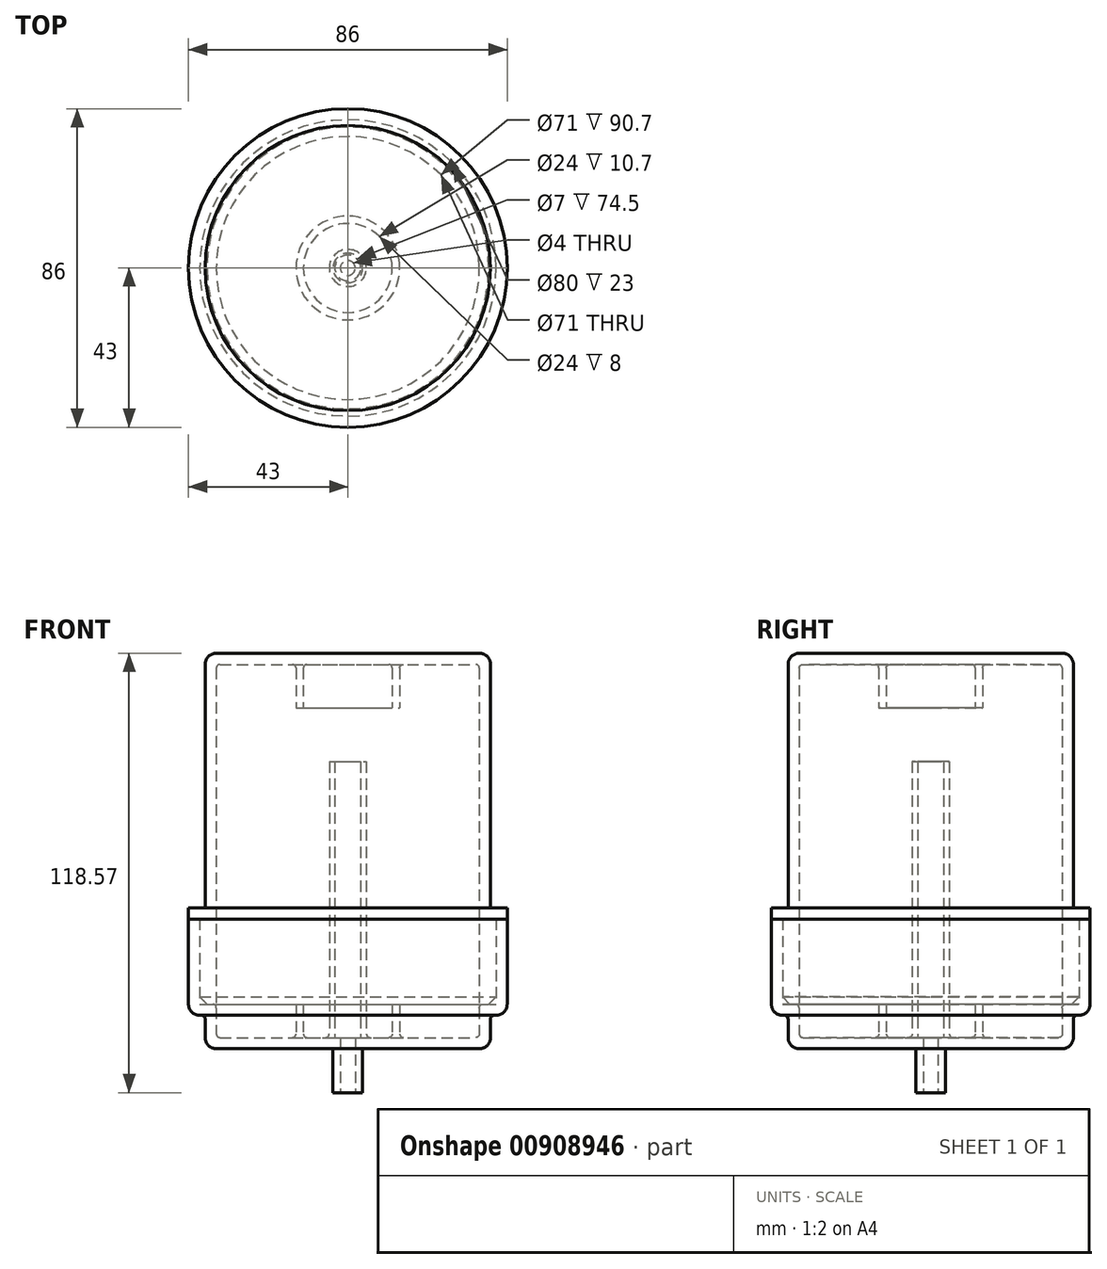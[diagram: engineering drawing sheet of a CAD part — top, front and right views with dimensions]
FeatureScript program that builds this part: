
annotation { "Feature Type Name" : "Feature", "Feature Type Description" : "" }
export const myFeature = defineFeature(function(context is Context, id is Id, definition is map)
    precondition{}
    {
        {
            var Q0;
            Q0=qCreatedBy(makeId("Front.planeOp"),FACE);
            var sketch = newSketch(context, id + "F0", { "sketchPlane" : qUnion([Q0])});
            skLineSegment(sketch, "E0", {"start": v(0, 0) * mm, "end": v(0, 111.4) * mm, "construction": true});
            skLineSegment(sketch, "E1", {"start": v(12, 1) * mm, "end": v(12, 9) * mm});
            skLineSegment(sketch, "E2", {"start": v(12, 9) * mm, "end": v(14, 9) * mm});
            skLineSegment(sketch, "E3", {"start": v(14, 9) * mm, "end": v(14, 1) * mm});
            skLineSegment(sketch, "E4", {"start": v(15, 0) * mm, "end": v(34.5, 0) * mm});
            skLineSegment(sketch, "E5", {"start": v(35.5, 1) * mm, "end": v(35.5, 8) * mm});
            skLineSegment(sketch, "E6", {"start": v(36.5, 9) * mm, "end": v(40, 9) * mm});
            skLineSegment(sketch, "E7", {"start": v(35.5, -3) * mm, "end": v(4, -3) * mm});
            skLineSegment(sketch, "E8", {"start": v(40, 9) * mm, "end": v(40, 32) * mm});
            skLineSegment(sketch, "E9", {"start": v(40, 32) * mm, "end": v(43, 32) * mm});
            skLineSegment(sketch, "E10", {"start": v(43, 32) * mm, "end": v(43, 9) * mm});
            skLineSegment(sketch, "E11", {"start": v(40, 6) * mm, "end": v(39.5, 6) * mm});
            skLineSegment(sketch, "E12", {"start": v(38.5, 5) * mm, "end": v(38.5, 0) * mm});
            skLineSegment(sketch, "E13", {"start": v(3.5, 0) * mm, "end": v(3.5, 74.5) * mm});
            skLineSegment(sketch, "E14", {"start": v(3.5, 74.5) * mm, "end": v(5, 74.5) * mm});
            skLineSegment(sketch, "E15", {"start": v(5, 74.5) * mm, "end": v(5, 1) * mm});
            skLineSegment(sketch, "E16.trimOffspring", {"start": v(6, 0) * mm, "end": v(11, 0) * mm});
            skPoint(sketch, "E17.visualSharp", {"position": v(38.5, -3) * mm});
            skArc(sketch, "E17.filletArc", {"start": v(35.5, -3) * mm, "mid": v(37.62, -2.12) * mm, "end": v(38.5, 0) * mm});
            skPoint(sketch, "E18.visualSharp", {"position": v(43, 6) * mm});
            skArc(sketch, "E18.filletArc", {"start": v(40, 6) * mm, "mid": v(42.12, 6.88) * mm, "end": v(43, 9) * mm});
            skPoint(sketch, "E19.visualSharp", {"position": v(5, 0) * mm});
            skArc(sketch, "E19.filletArc", {"start": v(5, 1) * mm, "mid": v(5.3, 0.3) * mm, "end": v(6, 0) * mm});
            skPoint(sketch, "E20.visualSharp", {"position": v(12, 0) * mm});
            skArc(sketch, "E20.filletArc", {"start": v(11, 0) * mm, "mid": v(11.7, 0.3) * mm, "end": v(12, 1) * mm});
            skPoint(sketch, "E21.visualSharp", {"position": v(14, 0) * mm});
            skArc(sketch, "E21.filletArc", {"start": v(14, 1) * mm, "mid": v(14.3, 0.3) * mm, "end": v(15, 0) * mm});
            skPoint(sketch, "E22.visualSharp", {"position": v(35.5, 9) * mm});
            skArc(sketch, "E22.filletArc", {"start": v(36.5, 9) * mm, "mid": v(35.8, 8.7) * mm, "end": v(35.5, 8) * mm});
            skPoint(sketch, "E23.visualSharp", {"position": v(38.5, 6) * mm});
            skArc(sketch, "E23.filletArc", {"start": v(39.5, 6) * mm, "mid": v(38.8, 5.7) * mm, "end": v(38.5, 5) * mm});
            skArc(sketch, "E24.filletArc", {"start": v(34.5, 0) * mm, "mid": v(35.2, 0.3) * mm, "end": v(35.5, 1) * mm});
            skLineSegment(sketch, "E25", {"start": v(2, -14.87) * mm, "end": v(4, -14.87) * mm});
            skLineSegment(sketch, "E26", {"start": v(4, -14.87) * mm, "end": v(4, -3) * mm});
            skLineSegment(sketch, "E27", {"start": v(2, -14.87) * mm, "end": v(2, -3) * mm});
            skLineSegment(sketch, "E28", {"start": v(3.5, 0) * mm, "end": v(2, 0) * mm});
            skLineSegment(sketch, "E29", {"start": v(2, -3) * mm, "end": v(2, 0) * mm});
            skLineSegment(sketch, "E30", {"start": v(0, 0) * mm, "end": v(2, 0) * mm});
            skSolve(sketch);
        }
        {
            var Q0;
            Q0=makeQuery(id+"F0.imprint","IMPRINT",FACE,{"disambiguationData":[TD([[makeQuery(id+"F0.imprint","IMPRINT",EDGE,{"derivedFrom":sQuery(id+"F0.wireOp",EDGE,"E1")}),-1.0]])]});
            var Q1;
            Q1=sQuery(id+"F0.wireOp",EDGE,"E0");
            revolve(context, id + "F1", {"surfaceOperationType" : NewSurfaceOperationType.NEW, "entities" : qUnion([Q0]), "axis" : qUnion([Q1]), "revolveType" : RevolveType.FULL});
        }
        {
            var Q0;
            Q0=qCreatedBy(makeId("Front.planeOp"),FACE);
            var sketch = newSketch(context, id + "F2", { "sketchPlane" : qUnion([Q0])});
            skLineSegment(sketch, "E31.0", {"start": v(36.5, 9) * mm, "end": v(38, 9) * mm});
            skLineSegment(sketch, "E31.1", {"start": v(40, 11) * mm, "end": v(40, 32) * mm});
            skLineSegment(sketch, "E32", {"start": v(36.5, 9) * mm, "end": v(35.5, 9) * mm});
            skLineSegment(sketch, "E33", {"start": v(35.5, 9) * mm, "end": v(35.5, 99.7) * mm});
            skLineSegment(sketch, "E34.0", {"start": v(40, 32) * mm, "end": v(43, 32) * mm});
            skLineSegment(sketch, "E35", {"start": v(38, 9) * mm, "end": v(40, 11) * mm});
            skPoint(sketch, "E36.orphan", {"position": v(40, 9) * mm});
            skLineSegment(sketch, "E37.0", {"start": v(35.5, 1) * mm, "end": v(35.5, 8) * mm, "construction": true});
            skLineSegment(sketch, "E38", {"start": v(43, 32) * mm, "end": v(43, 35) * mm});
            skLineSegment(sketch, "E39.0", {"start": v(14, 9) * mm, "end": v(14, 1) * mm, "construction": true});
            skLineSegment(sketch, "E39.1", {"start": v(12, 1) * mm, "end": v(12, 9) * mm, "construction": true});
            skLineSegment(sketch, "E40", {"start": v(34.5, 100.7) * mm, "end": v(15, 100.7) * mm});
            skLineSegment(sketch, "E41", {"start": v(14, 99.7) * mm, "end": v(14, 89) * mm});
            skLineSegment(sketch, "E42", {"start": v(14, 89) * mm, "end": v(12, 89) * mm});
            skLineSegment(sketch, "E43", {"start": v(12, 89) * mm, "end": v(12, 99.7) * mm});
            skLineSegment(sketch, "E44", {"start": v(11, 100.7) * mm, "end": v(0, 100.7) * mm});
            skLineSegment(sketch, "E45", {"start": v(0, 100.7) * mm, "end": v(0, 103.7) * mm});
            skLineSegment(sketch, "E46", {"start": v(0, 103.7) * mm, "end": v(35.5, 103.7) * mm});
            skLineSegment(sketch, "E47", {"start": v(43, 35) * mm, "end": v(38.5, 35) * mm});
            skLineSegment(sketch, "E48", {"start": v(38.5, 35) * mm, "end": v(38.5, 100.7) * mm});
            skPoint(sketch, "E49.visualSharp", {"position": v(35.5, 100.7) * mm});
            skArc(sketch, "E49.filletArc", {"start": v(35.5, 99.7) * mm, "mid": v(35.2, 100.4) * mm, "end": v(34.5, 100.7) * mm});
            skPoint(sketch, "E50.visualSharp", {"position": v(14, 100.7) * mm});
            skArc(sketch, "E50.filletArc", {"start": v(15, 100.7) * mm, "mid": v(14.3, 100.4) * mm, "end": v(14, 99.7) * mm});
            skPoint(sketch, "E51.visualSharp", {"position": v(12, 100.7) * mm});
            skArc(sketch, "E51.filletArc", {"start": v(12, 99.7) * mm, "mid": v(11.7, 100.4) * mm, "end": v(11, 100.7) * mm});
            skPoint(sketch, "E52.visualSharp", {"position": v(38.5, 103.7) * mm});
            skArc(sketch, "E52.filletArc", {"start": v(38.5, 100.7) * mm, "mid": v(37.62, 102.82) * mm, "end": v(35.5, 103.7) * mm});
            skSolve(sketch);
        }
        {
            var Q0;
            Q0 = qSketchRegion(id + "F2", true);
            var Q1;
            Q1=sQuery(id+"F0.wireOp",EDGE,"E0");
            revolve(context, id + "F3", {"surfaceOperationType" : NewSurfaceOperationType.NEW, "entities" : qUnion([Q0]), "axis" : qUnion([Q1]), "revolveType" : RevolveType.FULL});
        }
    });
